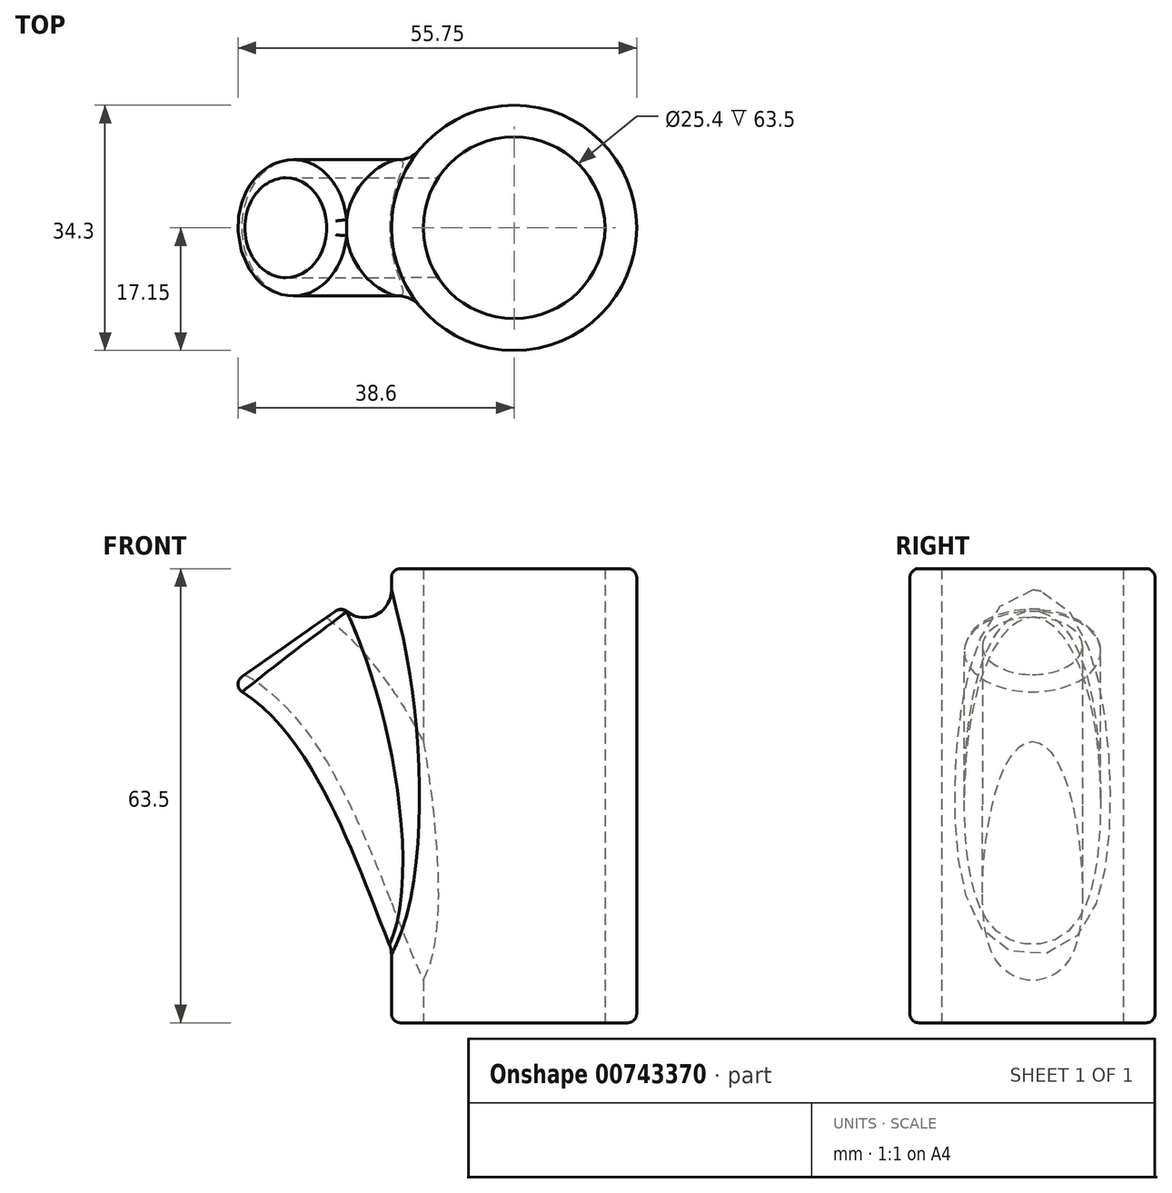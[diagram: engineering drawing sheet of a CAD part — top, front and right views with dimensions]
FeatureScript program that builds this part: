
annotation { "Feature Type Name" : "Feature", "Feature Type Description" : "" }
export const myFeature = defineFeature(function(context is Context, id is Id, definition is map)
    precondition{}
    {
        {
            var Q0;
            Q0=qCreatedBy(makeId("Top.planeOp"),FACE);
            var sketch = newSketch(context, id + "F0", { "sketchPlane" : qUnion([Q0])});
            skCircle(sketch, "E0", {"center": v(0, 0) * mm, "radius": 12.7 * mm});
            skCircle(sketch, "E1", {"center": v(0, 0) * mm, "radius": 17.15 * mm});
            skSolve(sketch);
        }
        {
            var Q0;
            Q0=makeQuery(id+"F0.imprint","IMPRINT",FACE,{"disambiguationData":[TD([[makeQuery(id+"F0.imprint","IMPRINT",EDGE,{"derivedFrom":sQuery(id+"F0.wireOp",EDGE,"E0")}),-1.0]])]});
            extrude(context, id + "F1", {"entities" : qUnion([Q0]), "depth" : 63.5 * mm, "offsetDistance" : 25.4 * mm});
        }
        {
            var Q0;
            Q0=qCreatedBy(makeId("Right.planeOp"),FACE);
            cPlane(context, id + "F2", {"entities" : qUnion([Q0]), "cplaneType" : CPlaneType.OFFSET, "offset" : 16.76 * mm, "oppositeDirection" : true, "width" : 152.4 * mm, "height" : 152.4 * mm});
        }
        {
            var Q0;
            Q0=qCreatedBy(id+"F2.planeOp",FACE);
            var sketch = newSketch(context, id + "F3", { "sketchPlane" : qUnion([Q0])});
            skLineSegment(sketch, "E2", {"start": v(45.22, 63.3) * mm, "end": v(-44.35, 63.3) * mm});
            skSolve(sketch);
        }
        {
            var Q0;
            Q0=sQuery(id+"F3.wireOp",EDGE,"E2");
            cPlane(context, id + "F4", {"entities" : qUnion([Q0]), "cplaneType" : CPlaneType.LINE_ANGLE, "offset" : 25.4 * mm, "angle" : 35 * degree, "width" : 152.4 * mm, "height" : 152.4 * mm});
        }
        {
            var Q0;
            Q0=qCreatedBy(id+"F4.planeOp",FACE);
            var sketch = newSketch(context, id + "F5", { "sketchPlane" : qUnion([Q0])});
            skCircle(sketch, "E3", {"center": v(4.09, 0) * mm, "radius": 6.99 * mm});
            skCircle(sketch, "E4", {"center": v(4.09, 0) * mm, "radius": 9.53 * mm});
            skSolve(sketch);
        }
        {
            var Q0;
            {var subQ0=sQuery(id+"F5.wireOp",EDGE,"E4");Q0=makeQuery(id+"FPSWW7IS3d8COEw_1.boolean.opBoolean","SPLIT",FACE,{"disambiguationData":[TD([makeQuery(id+"F1.opExtrude","SWEPT_FACE",FACE,{"disambiguationData":[OSD([sQuery(id+"F0.wireOp",EDGE,"E1")])]})])],"derivedFrom":makeQuery(id+"FPSWW7IS3d8COEw_1.opExtrude","SWEPT_FACE",FACE,{"disambiguationData":[OSD([subQ0])]})});}
            var Q1;
            Q1=makeQuery(id+"F1.opExtrude","CAP_EDGE",EDGE,{"disambiguationData":[OSD([sQuery(id+"F0.wireOp",EDGE,"E1")])],"isStart":false});
            var Q2;
            Q2=makeQuery(id+"F1.opExtrude","CAP_EDGE",EDGE,{"disambiguationData":[OSD([sQuery(id+"F0.wireOp",EDGE,"E1")])],"isStart":true});
            fillet(context, id + "F6", {"entities" : qUnion([Q0, Q1, Q2]), "radius" : 1.27 * mm, "tangentPropagation" : true, "allowEdgeOverflow" : false});
        }
        {
            var Q0;
            Q0=makeQuery(id+"F1.opExtrude","CAP_FACE",FACE,{"disambiguationData":[OSD([sQuery(id+"F0.wireOp",EDGE,"E0"),sQuery(id+"F0.wireOp",EDGE,"E1")])],"isStart":true});
            var sketch = newSketch(context, id + "F7", { "sketchPlane" : qUnion([Q0])});
            skCircle(sketch, "E5", {"center": v(0, 0) * mm, "radius": 12.7 * mm});
            skSolve(sketch);
        }
        {
            var Q0;
            Q0=qSketchRegion(id+"F7",true);
            extrude(context, id + "F8", {"entities" : qUnion([Q0]), "operationType" : NewBodyOperationType.REMOVE, "oppositeDirection" : true, "depth" : 68.07 * mm, "offsetDistance" : 25.4 * mm});
        }
        {
            var Q0;
            Q0=qCreatedBy(makeId("Front.planeOp"),FACE);
            var sketch = newSketch(context, id + "F9", { "sketchPlane" : qUnion([Q0])});
            skPoint(sketch, "E6", {"position": v(-31.9, 52.7) * mm});
            skFitSpline(sketch, "E7", {"points": [v(-32.02, 52.18) * mm, v(-2.01, 0) * mm], "startDerivative": vector(50.82, -36.2) * mm, "endDerivative": vector(26.13, -28.64) * mm});
            skSolve(sketch);
        }
        {
            var Q0;
            Q0=makeQuery(id+"F5.imprint","IMPRINT",FACE,{"disambiguationData":[TD([[makeQuery(id+"F5.imprint","IMPRINT",EDGE,{"derivedFrom":sQuery(id+"F5.wireOp",EDGE,"E3")}),-1.0]])]});
            var Q1;
            Q1=sQuery(id+"F9.wireOp",EDGE,"E7");
            sweep(context, id + "F10", {"operationType" : NewBodyOperationType.ADD, "profiles" : qUnion([Q0]), "path" : qUnion([Q1])});
        }
        {
            var Q0;
            Q0=makeQuery(id+"F1.opExtrude","CAP_FACE",FACE,{"disambiguationData":[OSD([sQuery(id+"F0.wireOp",EDGE,"E0"),sQuery(id+"F0.wireOp",EDGE,"E1")])],"isStart":true});
            var sketch = newSketch(context, id + "F11", { "sketchPlane" : qUnion([Q0])});
            skCircle(sketch, "E8", {"center": v(0, 0) * mm, "radius": 12.7 * mm});
            skSolve(sketch);
        }
        {
            var Q0;
            Q0 = qSketchRegion(id + "F11", true);
            extrude(context, id + "F12", {"entities" : qUnion([Q0]), "operationType" : NewBodyOperationType.REMOVE, "oppositeDirection" : true, "depth" : 47.75 * mm, "offsetDistance" : 25.4 * mm, "hasSecondDirection" : true, "secondDirectionOppositeDirection" : false, "secondDirectionDepth" : 25.4 * mm});
        }
        {
            var Q0;
            Q0=makeQuery(id+"F10.boolean.opBoolean","INTERSECT",EDGE,{"derivedFrom":[makeQuery(id+"F1.opExtrude","SWEPT_FACE",FACE,{"disambiguationData":[OSD([sQuery(id+"F0.wireOp",EDGE,"E1")])]}),makeQuery(id+"F10.opSweep","SWEPT_FACE",FACE,{"disambiguationData":[OSD([sQuery(id+"F5.wireOp",EDGE,"E4"),sQuery(id+"F9.wireOp",EDGE,"E7")])]})]});
            fillet(context, id + "F13", {"entities" : qUnion([Q0]), "radius" : 3.8 * mm, "tangentPropagation" : true, "allowEdgeOverflow" : false});
        }
        {
            var Q0;
            Q0=makeQuery(id+"F10.opSweep","CAP_FACE",FACE,{"disambiguationData":[OSD([sQuery(id+"F5.wireOp",EDGE,"E3"),sQuery(id+"F5.wireOp",EDGE,"E4"),sQuery(id+"F9.wireOp",VERTEX,"E7.start")])],"isStart":true});
            var sketch = newSketch(context, id + "F14", { "sketchPlane" : qUnion([Q0])});
            skCircle(sketch, "E9", {"center": v(4.09, 0) * mm, "radius": 6.99 * mm});
            skSolve(sketch);
        }
        {
            var Q0;
            Q0=makeQuery(id+"F14.imprint","IMPRINT",FACE,{"disambiguationData":[TD([[makeQuery(id+"F14.imprint","IMPRINT",EDGE,{"derivedFrom":sQuery(id+"F14.wireOp",EDGE,"E9")}),-1.0]])]});
            var Q1;
            Q1=sQuery(id+"F9.wireOp",EDGE,"E7");
            sweep(context, id + "F15", {"operationType" : NewBodyOperationType.REMOVE, "profiles" : qUnion([Q0]), "path" : qUnion([Q1])});
        }
        {
            var Q0;
            Q0=makeQuery(id+"F10.opSweep","CAP_EDGE",EDGE,{"disambiguationData":[OSD([sQuery(id+"F5.wireOp",EDGE,"E4"),sQuery(id+"F9.wireOp",VERTEX,"E7.start")])],"isStart":true});
            fillet(context, id + "F16", {"entities" : qUnion([Q0]), "radius" : 1.27 * mm, "tangentPropagation" : true, "allowEdgeOverflow" : false});
        }
    });
